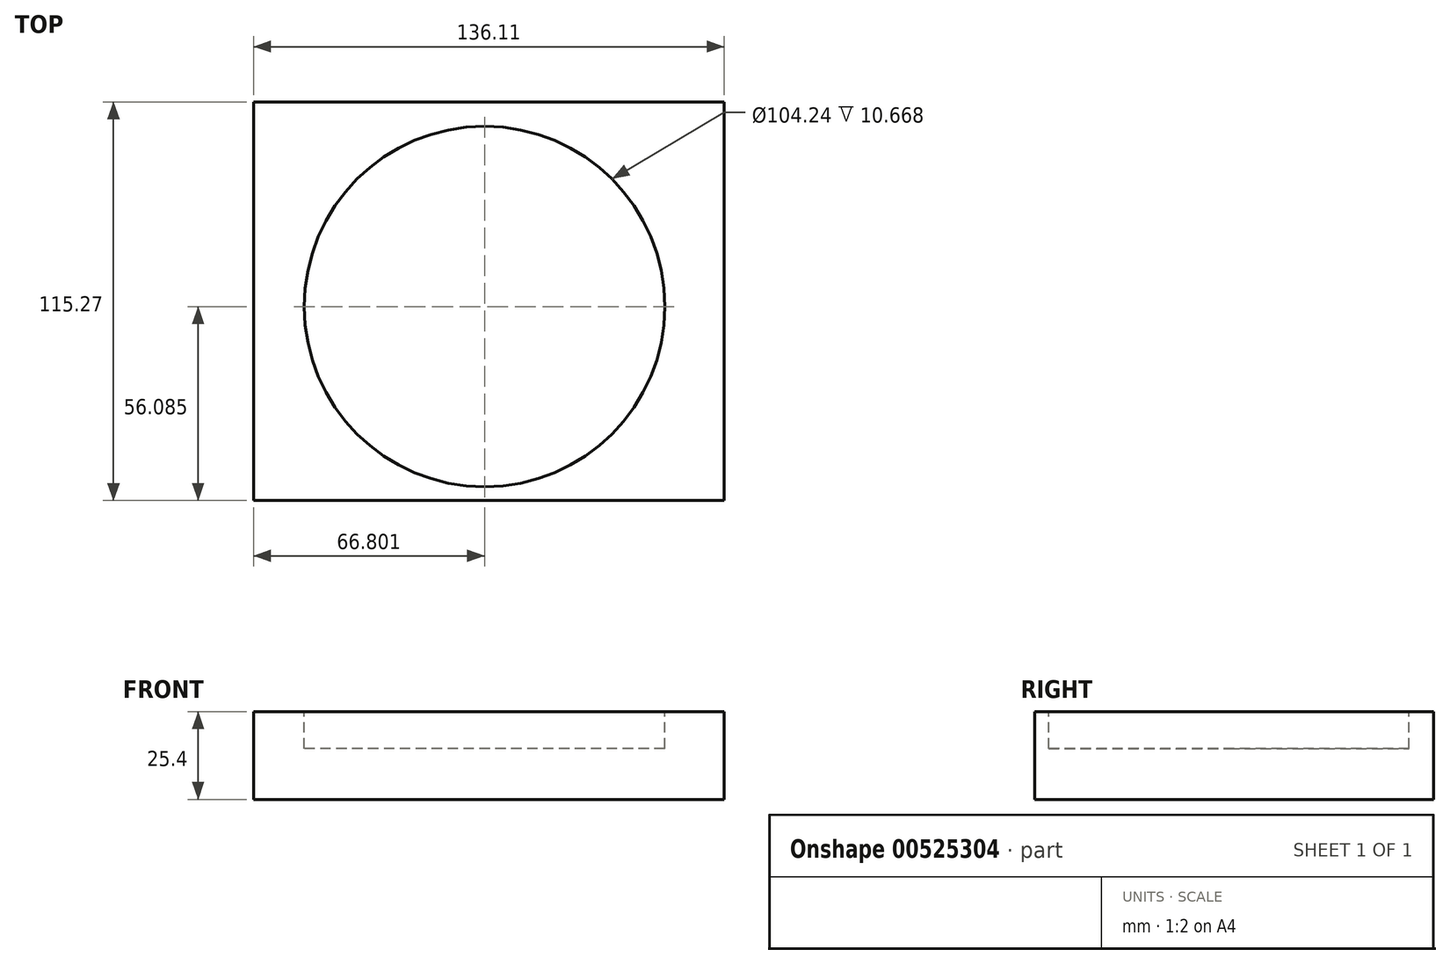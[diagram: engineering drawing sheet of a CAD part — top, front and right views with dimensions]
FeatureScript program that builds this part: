
annotation { "Feature Type Name" : "Feature", "Feature Type Description" : "" }
export const myFeature = defineFeature(function(context is Context, id is Id, definition is map)
    precondition{}
    {
        {
            var Q0;
            Q0=qCreatedBy(makeId("Top.planeOp"),FACE);
            var sketch = newSketch(context, id + "F0", { "sketchPlane" : qUnion([Q0])});
            skLineSegment(sketch, "E0.bottom", {"start": v(0, 0) * mm, "end": v(136.11, 0) * mm});
            skLineSegment(sketch, "E0.top", {"start": v(0, -115.27) * mm, "end": v(136.11, -115.27) * mm});
            skLineSegment(sketch, "E0.left", {"start": v(0, 0) * mm, "end": v(0, -115.27) * mm});
            skLineSegment(sketch, "E0.right", {"start": v(136.11, 0) * mm, "end": v(136.11, -115.27) * mm});
            skSolve(sketch);
        }
        {
            var Q0;
            Q0=makeQuery(id+"F0.imprint","IMPRINT",FACE,{"disambiguationData":[TD([[makeQuery(id+"F0.imprint","IMPRINT",EDGE,{"derivedFrom":sQuery(id+"F0.wireOp",EDGE,"E0.bottom")}),-1.0]])]});
            extrude(context, id + "F1", {"entities" : qUnion([Q0]), "depth" : 25.4 * mm, "offsetDistance" : 25.4 * mm});
        }
        {
            var Q0;
            Q0=makeQuery(id+"F1.opExtrude","CAP_FACE",FACE,{"disambiguationData":[OSD([sQuery(id+"F0.wireOp",EDGE,"E0.bottom"),sQuery(id+"F0.wireOp",EDGE,"E0.top"),sQuery(id+"F0.wireOp",EDGE,"E0.left"),sQuery(id+"F0.wireOp",EDGE,"E0.right")])],"isStart":false});
            var sketch = newSketch(context, id + "F2", { "sketchPlane" : qUnion([Q0])});
            skCircle(sketch, "E1", {"center": v(66.8, -59.18) * mm, "radius": 52.12 * mm});
            skSolve(sketch);
        }
        {
            var Q0;
            Q0=makeQuery(id+"F2.imprint","IMPRINT",FACE,{"disambiguationData":[TD([[makeQuery(id+"F2.imprint","IMPRINT",EDGE,{"derivedFrom":sQuery(id+"F2.wireOp",EDGE,"E1")}),1.0]])]});
            var Q1;
            Q1=sQuery(id+"F2.wireOp",EDGE,"E1");
            extrude(context, id + "F3", {"entities" : qUnion([Q0]), "operationType" : NewBodyOperationType.REMOVE, "surfaceEntities" : qUnion([Q1]), "oppositeDirection" : true, "depth" : 10.67 * mm, "offsetDistance" : 25.4 * mm});
        }
    });
